# Revit family: ALRB
name_source: partatom
category: Lighting Fixtures
units: mm (PartAtom-declared; Revit-internal decimal feet)

## family parameters
Always vertical = Yes
Cut with Voids When Loaded = No
Host = Ceiling
Light Source = Yes
OmniClass Number = 23.80.70.11.14.17
OmniClass Title = Direct/Indirect
Part Type = Normal
Room Calculation Point = No
Round Connector Dimension = Use Diameter
Shared = No

## types (8) — shared parameters
Assembly Code = D5020200
Color Filter = 16777215
Description = Intellect Enabled LED ALLURA Linear Pendant Type B
Dimming Lamp Color Temperature Shift = <None>
Housing Finish = Metal - Viscor - White
Lamp = LED
Lens Finsih = Acrylic - Viscor - Frosted Round
Manufacturer = VISIONEERING by VISCOR
Model = ALRB
Tilt Angle = 180.00°
URL = https://www.viscor.com
Voltage = 120 V
Width = 0' - 6 1/8"

## per-type parameters (varying)
| type | Apparent Load | Emit from Line Length | Lamp Wattage | Length | Photometric Web File |
| ALRB48-LED840K050LUNV | 38 VA | 3' - 9" | 38 VA | 3' - 9" | ALRB48-LED840K050LUNV.ies |
| ALRB96-LED840K080LUNV | 60 VA | 7' - 5" | 60 VA | 7' - 5" | ALRB96-LED840K80LUNV.ies |
| ALRB48-LED840K035LUNV | 26 VA | 3' - 9" | 26 VA | 3' - 9" | ALRB48-LED840K035LUNV.ies |
| ALRB48-LED840K040LUNV | 30 VA | 3' - 9" | 30 VA | 3' - 9" | ALRB48-LED840K040LUNV.ies |
| ALRB96-LED840K070LUNV | 53 VA | 3' - 9" | 53 VA | 3' - 9" | ALRB96-LED840K070LUNV.ies |
| ALRB96-LED840K100LUNV | 76 VA | 3' - 9" | 76 VA | 3' - 9" | ALRB96-LED840K100LUNV.ies |
| ALRB96-LED840K120LUNV | 94 VA | 3' - 9" | 94 VA | 3' - 9" | ALRB96-LED840K120LUNV.ies |
| ALRB48-LED840K060LUNV | 47 VA | 3' - 9" | 47 VA | 3' - 9" | ALRB48-LED840K060LUNV.ies |

## geometry (parser evidence)
native form markers: Sweep x3
no freeform markers — native parametric forms only
